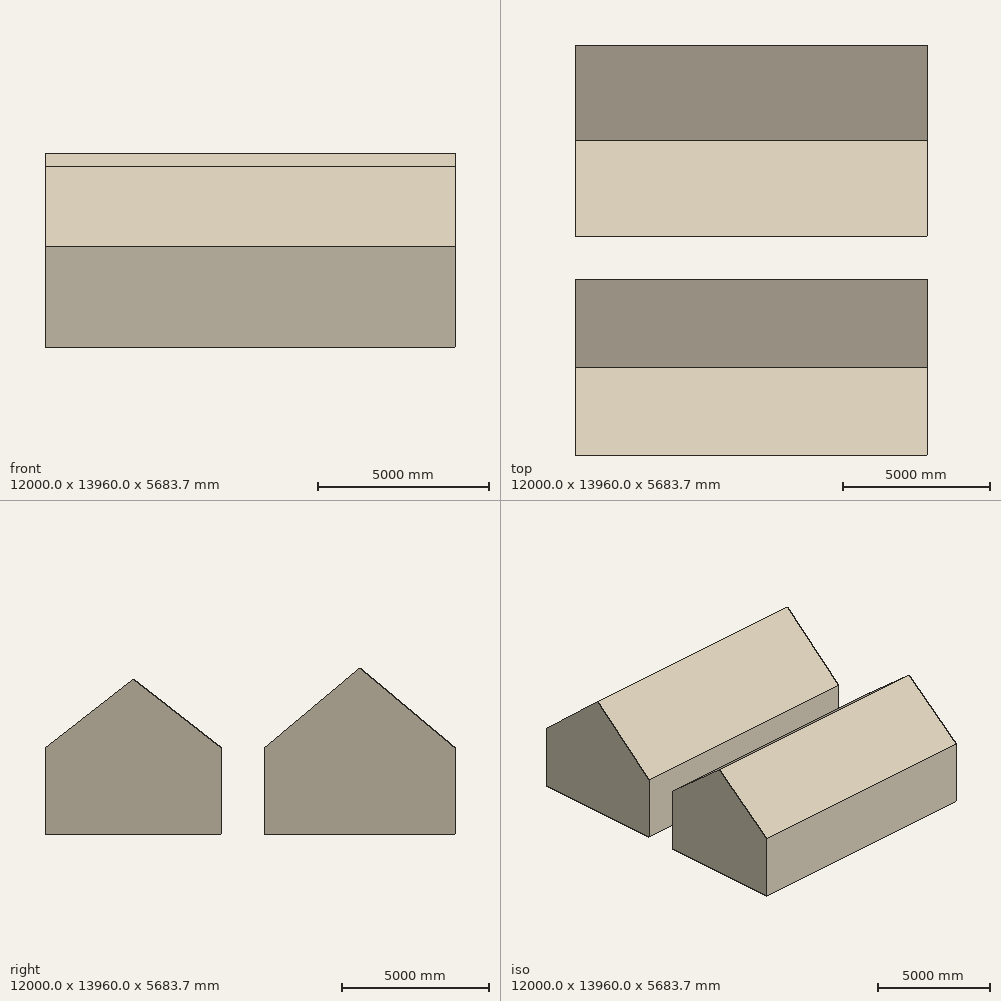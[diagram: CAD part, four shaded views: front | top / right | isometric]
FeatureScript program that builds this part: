
annotation { "Feature Type Name" : "Feature", "Feature Type Description" : "" }
export const myFeature = defineFeature(function(context is Context, id is Id, definition is map)
    precondition{}
    {
        {
            var Q0;
            Q0=qCreatedBy(makeId("Top.planeOp"),FACE);
            var sketch = newSketch(context, id + "F0", { "sketchPlane" : qUnion([Q0])});
            skLineSegment(sketch, "E0.bottom", {"start": v(6000, -3250) * mm, "end": v(-6000, -3250) * mm});
            skLineSegment(sketch, "E0.top", {"start": v(6000, 3250) * mm, "end": v(-6000, 3250) * mm});
            skLineSegment(sketch, "E0.left", {"start": v(6000, -3250) * mm, "end": v(6000, 3250) * mm});
            skLineSegment(sketch, "E0.right", {"start": v(-6000, -3250) * mm, "end": v(-6000, 3250) * mm});
            skPoint(sketch, "E0.middle", {"position": v(0, 0) * mm});
            skSolve(sketch);
        }
        {
            var Q0;
            Q0 = qSketchRegion(id + "F0", true);
            extrude(context, id + "F1", {"entities" : qUnion([Q0]), "depth" : 2800 * mm, "offsetDistance" : 25 * mm});
        }
        {
            var Q0;
            Q0=makeQuery(id+"F1.opExtrude","SWEPT_FACE",FACE,{"disambiguationData":[OSD([sQuery(id+"F0.wireOp",EDGE,"E0.right")])]});
            var sketch = newSketch(context, id + "F2", { "sketchPlane" : qUnion([Q0])});
            skLineSegment(sketch, "E1", {"start": v(-3250, 2800) * mm, "end": v(2254.27, 2800) * mm});
            skLineSegment(sketch, "E2", {"start": v(3250, 2800) * mm, "end": v(0, 5527.07) * mm});
            skPoint(sketch, "E2.endSnap0", {"position": v(0, 2800) * mm});
            skLineSegment(sketch, "E3", {"start": v(0, 5527.07) * mm, "end": v(-3250, 2800) * mm});
            skLineSegment(sketch, "E4", {"start": v(3250, 2800) * mm, "end": v(3250, 2400) * mm});
            skLineSegment(sketch, "E5", {"start": v(3250, 2400) * mm, "end": v(-3250, 2400) * mm});
            skLineSegment(sketch, "E6.top", {"start": v(3250, 2570) * mm, "end": v(-3250, 2570) * mm});
            skLineSegment(sketch, "E6.left", {"start": v(3250, 2400) * mm, "end": v(3250, 2570) * mm});
            skLineSegment(sketch, "E6.right", {"start": v(-3250, 2400) * mm, "end": v(-3250, 2570) * mm});
            skLineSegment(sketch, "E7.0", {"start": v(0, 5161.56) * mm, "end": v(-2978.9, 2661.97) * mm});
            skLineSegment(sketch, "E7.1", {"start": v(2814.4, 2800) * mm, "end": v(0, 5161.56) * mm});
            skLineSegment(sketch, "E8.0", {"start": v(0, 5683.72) * mm, "end": v(-3178.34, 3016.78) * mm});
            skLineSegment(sketch, "E8.1", {"start": v(3173.88, 3020.52) * mm, "end": v(0, 5683.72) * mm});
            skLineSegment(sketch, "E9", {"start": v(-3178.34, 3016.78) * mm, "end": v(-3408.16, 2823.94) * mm});
            skLineSegment(sketch, "E10", {"start": v(-3250, 2800) * mm, "end": v(-3479.81, 2607.16) * mm});
            skLineSegment(sketch, "E11", {"start": v(-3479.81, 2607.16) * mm, "end": v(-3408.16, 2823.94) * mm});
            skLineSegment(sketch, "E12", {"start": v(3173.88, 3020.52) * mm, "end": v(3403.7, 2827.69) * mm});
            skLineSegment(sketch, "E13", {"start": v(3250, 2800) * mm, "end": v(3479.81, 2607.16) * mm});
            skLineSegment(sketch, "E14", {"start": v(3479.81, 2607.16) * mm, "end": v(3403.7, 2827.69) * mm});
            skLineSegment(sketch, "E15", {"start": v(-2254.27, 3270) * mm, "end": v(-2254.27, 2570) * mm});
            skLineSegment(sketch, "E16", {"start": v(2254.27, 3270) * mm, "end": v(2254.27, 2570) * mm});
            skLineSegment(sketch, "E17.trimOffspring", {"start": v(2814.4, 2800) * mm, "end": v(3250, 2800) * mm});
            skLineSegment(sketch, "E18", {"start": v(-650, 4616.15) * mm, "end": v(650, 4616.15) * mm});
            skLineSegment(sketch, "E19", {"start": v(-3250, 2800) * mm, "end": v(-3250, 2956.65) * mm});
            skLineSegment(sketch, "E20", {"start": v(3250, 2800) * mm, "end": v(3250, 2956.65) * mm});
            skLineSegment(sketch, "E21.bottom", {"start": v(4709.97, 2958) * mm, "end": v(10709.97, 2958) * mm});
            skLineSegment(sketch, "E21.top", {"start": v(4709.97, 0) * mm, "end": v(10709.97, 0) * mm});
            skLineSegment(sketch, "E21.left", {"start": v(4709.97, 2958) * mm, "end": v(4709.97, 0) * mm});
            skLineSegment(sketch, "E21.right", {"start": v(10709.97, 2958) * mm, "end": v(10709.97, 0) * mm});
            skLineSegment(sketch, "E22", {"start": v(4709.97, 2958) * mm, "end": v(7709.97, 5301.86) * mm});
            skPoint(sketch, "E22.endSnap0", {"position": v(7709.97, 2958) * mm});
            skLineSegment(sketch, "E23", {"start": v(7709.97, 5301.86) * mm, "end": v(10709.97, 2958) * mm});
            skSolve(sketch);
        }
        {
            var Q0;
            Q0=makeQuery(id+"F2.imprint","IMPRINT",FACE,{"disambiguationData":[TD([[makeQuery(id+"F2.imprint","IMPRINT",EDGE,{"derivedFrom":sQuery(id+"F2.wireOp",EDGE,"owdtdeJN-tYeO-8T4P-i78H-aunVc4Q9wc5y.bottom")}),-1.0]])]});
            var Q1;
            Q1=makeQuery(id+"F2.imprint","IMPRINT",FACE,{"disambiguationData":[TD([[makeQuery(id+"F2.imprint","IMPRINT",EDGE,{"derivedFrom":sQuery(id+"F2.wireOp",EDGE,"owdtdeJN-tYeO-8T4P-i78H-aunVc4Q9wc5y.bottom")}),1.0]])]});
            var Q2;
            {var subQ0=sQuery(id+"F2.wireOp",EDGE,"E15");var subQ1=sQuery(id+"F2.wireOp",EDGE,"E1");var subQ2=makeQuery(id+"F2.imprint","INTERSECT",VERTEX,{"derivedFrom":[subQ1,subQ0]});Q2=makeQuery(id+"F2.imprint","IMPRINT",FACE,{"disambiguationData":[TD([[makeQuery(id+"F2.imprint","IMPRINT",EDGE,{"disambiguationData":[TD([[subQ2,-1.0]])],"derivedFrom":subQ1}),-1.0]])]});}
            var Q3;
            Q3=makeQuery(id+"F2.imprint","IMPRINT",FACE,{"disambiguationData":[TD([[makeQuery(id+"F2.imprint","IMPRINT",EDGE,{"derivedFrom":sQuery(id+"F2.wireOp",EDGE,"E2")}),-1.0]])]});
            var Q4;
            {var subQ0=sQuery(id+"F2.wireOp",EDGE,"E7.1");var subQ3=sQuery(id+"F2.wireOp",EDGE,"E16");var subQ4=makeQuery(id+"F2.imprint","INTERSECT",VERTEX,{"derivedFrom":[subQ0,subQ3]});Q4=makeQuery(id+"F2.imprint","IMPRINT",FACE,{"disambiguationData":[TD([[makeQuery(id+"F2.imprint","IMPRINT",EDGE,{"disambiguationData":[TD([[subQ4,1.0]])],"derivedFrom":subQ0}),1.0]])]});}
            var Q5;
            {var subQ0=sQuery(id+"F2.wireOp",EDGE,"E15");var subQ1=sQuery(id+"F2.wireOp",EDGE,"E1");var subQ2=makeQuery(id+"F2.imprint","INTERSECT",VERTEX,{"derivedFrom":[subQ1,subQ0]});Q5=makeQuery(id+"F2.imprint","IMPRINT",FACE,{"disambiguationData":[TD([[makeQuery(id+"F2.imprint","IMPRINT",EDGE,{"disambiguationData":[TD([[subQ2,-1.0]])],"derivedFrom":subQ1}),1.0]])]});}
            var Q6;
            {var subQ6=sQuery(id+"F2.wireOp",EDGE,"E4");Q6=makeQuery(id+"F2.imprint","IMPRINT",FACE,{"disambiguationData":[TD([[makeQuery(id+"F2.imprint","IMPRINT",EDGE,{"derivedFrom":subQ6}),-1.0]])]});}
            var Q7;
            Q7=makeQuery(id+"F2.imprint","IMPRINT",FACE,{"disambiguationData":[TD([[makeQuery(id+"F2.imprint","IMPRINT",EDGE,{"derivedFrom":sQuery(id+"F2.wireOp",EDGE,"E5")}),-1.0]])]});
            var Q8;
            Q8=makeQuery(id+"F2.imprint","IMPRINT",FACE,{"disambiguationData":[TD([[makeQuery(id+"F2.imprint","IMPRINT",EDGE,{"derivedFrom":sQuery(id+"F2.wireOp",EDGE,"E2")}),1.0]])]});
            var Q9;
            {var subQ3=sQuery(id+"F2.wireOp",EDGE,"E18");Q9=makeQuery(id+"F2.imprint","IMPRINT",FACE,{"disambiguationData":[TD([[makeQuery(id+"F2.imprint","IMPRINT",EDGE,{"derivedFrom":subQ3}),1.0]])]});}
            var Q10;
            {var subQ3=sQuery(id+"F2.wireOp",EDGE,"E18");Q10=makeQuery(id+"F2.imprint","IMPRINT",FACE,{"disambiguationData":[TD([[makeQuery(id+"F2.imprint","IMPRINT",EDGE,{"derivedFrom":subQ3}),-1.0]])]});}
            var Q11;
            Q11=makeQuery(id+"F2.imprint","IMPRINT",FACE,{"disambiguationData":[TD([[makeQuery(id+"F2.imprint","IMPRINT",EDGE,{"derivedFrom":sQuery(id+"F2.wireOp",EDGE,"E21.bottom")}),1.0]])]});
            var Q12;
            Q12=makeQuery(id+"F2.imprint","IMPRINT",FACE,{"disambiguationData":[TD([[makeQuery(id+"F2.imprint","IMPRINT",EDGE,{"derivedFrom":sQuery(id+"F2.wireOp",EDGE,"E21.bottom")}),-1.0]])]});
            extrude(context, id + "F3", {"entities" : qUnion([Q0, Q1, Q2, Q3, Q4, Q5, Q6, Q7, Q8, Q9, Q10, Q11, Q12]), "operationType" : NewBodyOperationType.ADD, "oppositeDirection" : true, "depth" : 12000 * mm, "offsetDistance" : 25 * mm});
        }
    });
